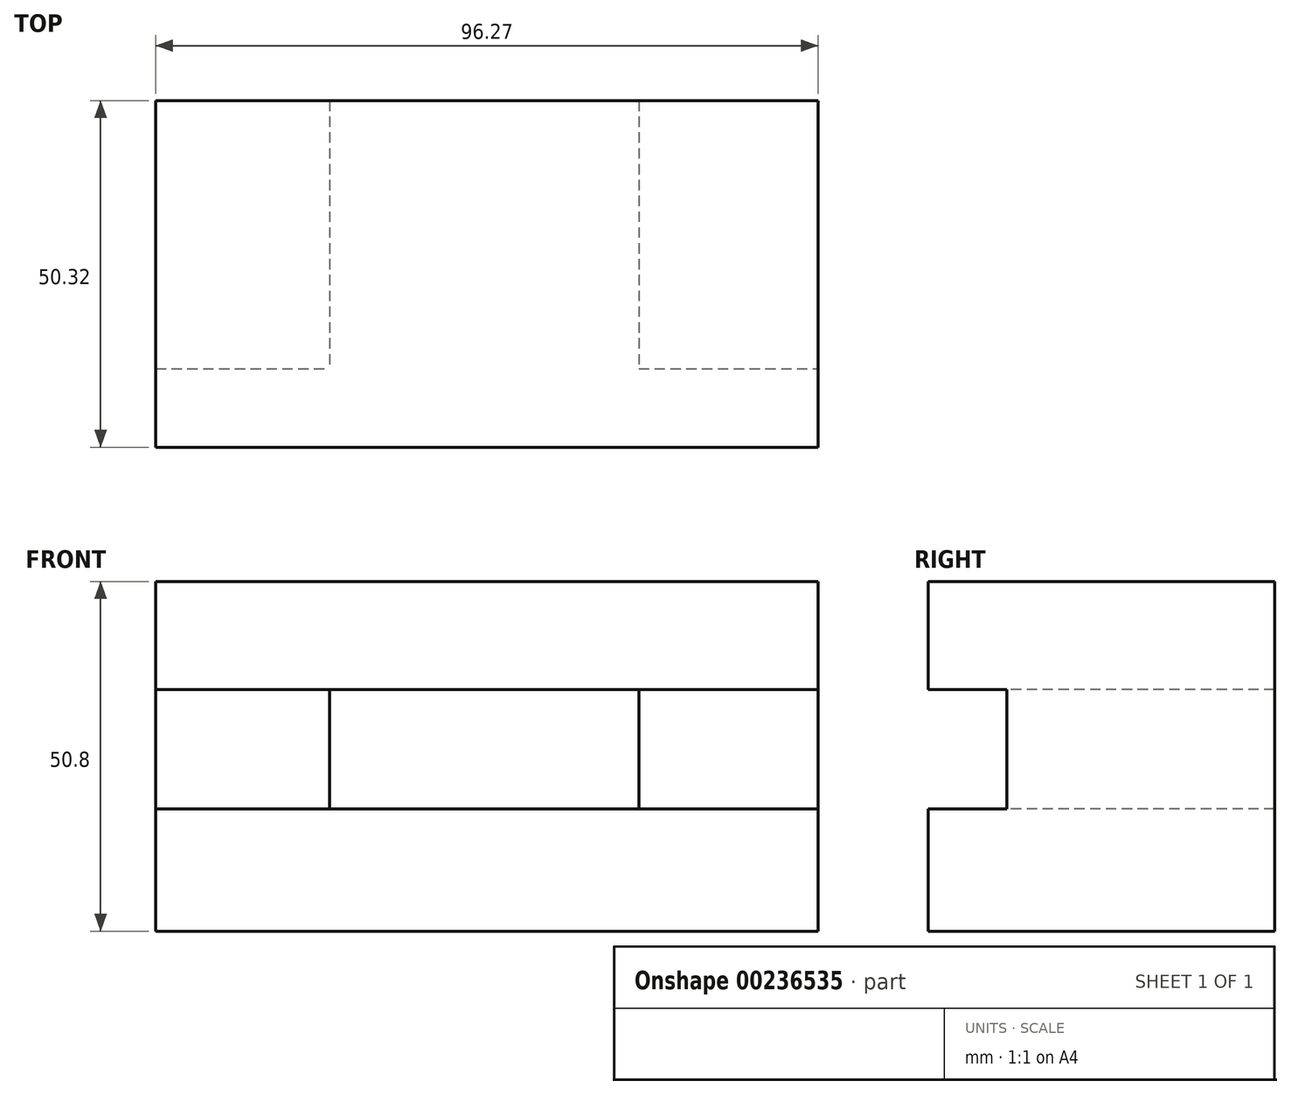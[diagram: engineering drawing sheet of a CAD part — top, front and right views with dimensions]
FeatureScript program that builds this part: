
annotation { "Feature Type Name" : "Feature", "Feature Type Description" : "" }
export const myFeature = defineFeature(function(context is Context, id is Id, definition is map)
    precondition{}
    {
        {
            var Q0;
            Q0=qCreatedBy(makeId("Top.planeOp"),FACE);
            var sketch = newSketch(context, id + "F0", { "sketchPlane" : qUnion([Q0])});
            skLineSegment(sketch, "E0.bottom", {"start": v(-42.07, 22.45) * mm, "end": v(54.2, 22.45) * mm});
            skLineSegment(sketch, "E0.top", {"start": v(-42.07, -27.87) * mm, "end": v(54.2, -27.87) * mm});
            skLineSegment(sketch, "E0.left", {"start": v(-42.07, 22.45) * mm, "end": v(-42.07, -27.87) * mm});
            skLineSegment(sketch, "E0.right", {"start": v(54.2, 22.45) * mm, "end": v(54.2, -27.87) * mm});
            skSolve(sketch);
        }
        {
            var Q0;
            Q0=makeQuery(id+"F0.imprint","IMPRINT",FACE,{"disambiguationData":[TD([[makeQuery(id+"F0.imprint","IMPRINT",EDGE,{"derivedFrom":sQuery(id+"F0.wireOp",EDGE,"E0.bottom")}),-1.0]])]});
            extrude(context, id + "F1", {"entities" : qUnion([Q0]), "depth" : 50.8 * mm});
        }
        {
            var Q0;
            Q0=makeQuery(id+"F1.opExtrude","SWEPT_FACE",FACE,{"disambiguationData":[OSD([sQuery(id+"F0.wireOp",EDGE,"E0.top")])]});
            var sketch = newSketch(context, id + "F2", { "sketchPlane" : qUnion([Q0])});
            skLineSegment(sketch, "E1.bottom", {"start": v(-42.07, 35.08) * mm, "end": v(54.2, 35.08) * mm});
            skLineSegment(sketch, "E1.top", {"start": v(-42.07, 17.79) * mm, "end": v(54.2, 17.79) * mm});
            skLineSegment(sketch, "E1.left", {"start": v(-42.07, 35.08) * mm, "end": v(-42.07, 17.79) * mm});
            skLineSegment(sketch, "E1.right", {"start": v(54.2, 35.08) * mm, "end": v(54.2, 17.79) * mm});
            skSolve(sketch);
        }
        {
            var Q0;
            Q0=makeQuery(id+"F2.imprint","IMPRINT",FACE,{"disambiguationData":[TD([[makeQuery(id+"F2.imprint","IMPRINT",EDGE,{"derivedFrom":sQuery(id+"F2.wireOp",EDGE,"E1.bottom")}),-1.0]])]});
            extrude(context, id + "F3", {"entities" : qUnion([Q0]), "operationType" : NewBodyOperationType.REMOVE, "oppositeDirection" : true, "depth" : 11.43 * mm});
        }
        {
            var Q0;
            Q0=makeQuery(id+"F3.boolean.opBoolean","COPY",FACE,{"derivedFrom":makeQuery(id+"F3.opExtrude","CAP_FACE",FACE,{"disambiguationData":[OSD([sQuery(id+"F2.wireOp",EDGE,"E1.bottom"),sQuery(id+"F2.wireOp",EDGE,"E1.top"),sQuery(id+"F2.wireOp",EDGE,"E1.left"),sQuery(id+"F2.wireOp",EDGE,"E1.right")])],"isStart":false})});
            var sketch = newSketch(context, id + "F4", { "sketchPlane" : qUnion([Q0])});
            skLineSegment(sketch, "E2.bottom", {"start": v(-16.78, 35.08) * mm, "end": v(28.13, 35.08) * mm});
            skLineSegment(sketch, "E2.top", {"start": v(-16.78, 17.79) * mm, "end": v(28.13, 17.79) * mm});
            skLineSegment(sketch, "E2.left", {"start": v(-16.78, 35.08) * mm, "end": v(-16.78, 17.79) * mm});
            skLineSegment(sketch, "E2.right", {"start": v(28.13, 35.08) * mm, "end": v(28.13, 17.79) * mm});
            skSolve(sketch);
        }
        {
            var Q0;
            Q0=makeQuery(id+"F4.imprint","IMPRINT",FACE,{"disambiguationData":[TD([[makeQuery(id+"F4.imprint","IMPRINT",EDGE,{"derivedFrom":sQuery(id+"F4.wireOp",EDGE,"E2.bottom")}),-1.0]])]});
            extrude(context, id + "F5", {"entities" : qUnion([Q0]), "operationType" : NewBodyOperationType.REMOVE, "oppositeDirection" : true, "depth" : 70.1 * mm});
        }
    });
